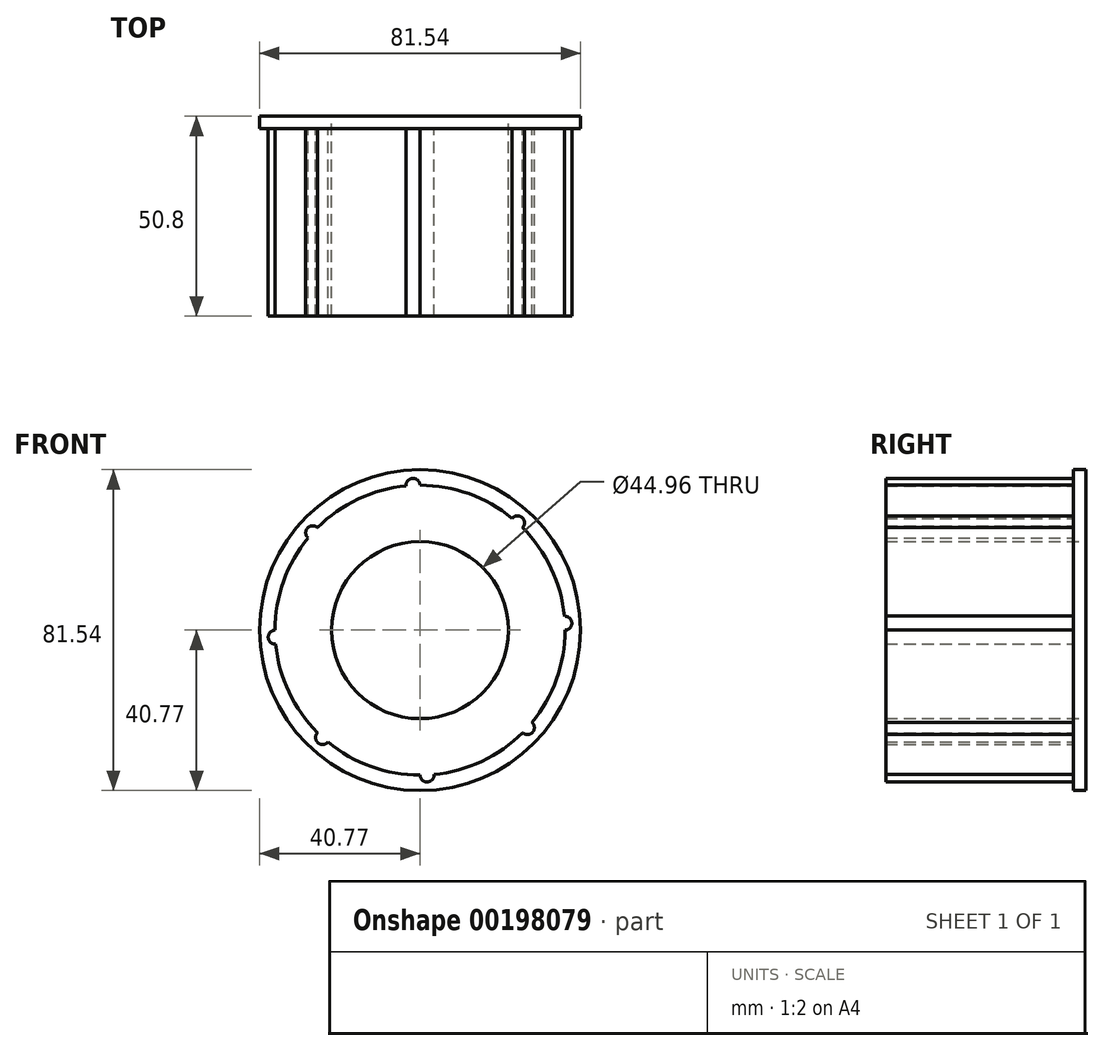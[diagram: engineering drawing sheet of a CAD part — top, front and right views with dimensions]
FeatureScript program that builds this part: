
annotation { "Feature Type Name" : "Feature", "Feature Type Description" : "" }
export const myFeature = defineFeature(function(context is Context, id is Id, definition is map)
    precondition{}
    {
        {
            var Q0;
            Q0=qCreatedBy(makeId("Front.planeOp"),FACE);
            var sketch = newSketch(context, id + "F0", { "sketchPlane" : qUnion([Q0])});
            skCircle(sketch, "E0", {"center": v(0, 0) * mm, "radius": 36.83 * mm});
            skCircle(sketch, "E1", {"center": v(0, 0) * mm, "radius": 22.48 * mm});
            skCircle(sketch, "E2", {"center": v(0, 0) * mm, "radius": 40.77 * mm});
            skArc(sketch, "E3", {"start": v(0, 36.83) * mm, "mid": v(-1.86, 38.56) * mm, "end": v(-3.55, 36.66) * mm});
            skArc(sketch, "E4.1.0", {"start": v(-26.04, 26.04) * mm, "mid": v(-28.59, 25.95) * mm, "end": v(-28.43, 23.41) * mm});
            skArc(sketch, "E4.2.0", {"start": v(-36.83, 0) * mm, "mid": v(-38.56, -1.86) * mm, "end": v(-36.66, -3.55) * mm});
            skArc(sketch, "E4.3.0", {"start": v(-26.04, -26.04) * mm, "mid": v(-25.95, -28.59) * mm, "end": v(-23.41, -28.43) * mm});
            skArc(sketch, "E4.4.0", {"start": v(0, -36.83) * mm, "mid": v(1.86, -38.56) * mm, "end": v(3.55, -36.66) * mm});
            skArc(sketch, "E4.5.0", {"start": v(26.04, -26.04) * mm, "mid": v(28.59, -25.95) * mm, "end": v(28.43, -23.41) * mm});
            skArc(sketch, "E4.6.0", {"start": v(36.83, 0) * mm, "mid": v(38.56, 1.86) * mm, "end": v(36.66, 3.55) * mm});
            skArc(sketch, "E4.7.0", {"start": v(26.04, 26.04) * mm, "mid": v(25.95, 28.59) * mm, "end": v(23.41, 28.43) * mm});
            skSolve(sketch);
        }
        {
            var Q0;
            Q0=makeQuery(id+"F0.imprint","IMPRINT",FACE,{"disambiguationData":[TD([[makeQuery(id+"F0.imprint","IMPRINT",EDGE,{"derivedFrom":sQuery(id+"F0.wireOp",EDGE,"E1")}),-1.0]])]});
            var Q1;
            {var subQ0=sQuery(id+"F0.wireOp",EDGE,"E3");Q1=makeQuery(id+"F0.imprint","IMPRINT",FACE,{"disambiguationData":[TD([[makeQuery(id+"F0.imprint","IMPRINT",EDGE,{"derivedFrom":subQ0}),1.0]])]});}
            var Q2;
            {var subQ0=sQuery(id+"F0.wireOp",EDGE,"E4.1.0");Q2=makeQuery(id+"F0.imprint","IMPRINT",FACE,{"disambiguationData":[TD([[makeQuery(id+"F0.imprint","IMPRINT",EDGE,{"derivedFrom":subQ0}),1.0]])]});}
            var Q3;
            {var subQ0=sQuery(id+"F0.wireOp",EDGE,"E4.2.0");Q3=makeQuery(id+"F0.imprint","IMPRINT",FACE,{"disambiguationData":[TD([[makeQuery(id+"F0.imprint","IMPRINT",EDGE,{"derivedFrom":subQ0}),1.0]])]});}
            var Q4;
            {var subQ0=sQuery(id+"F0.wireOp",EDGE,"E4.6.0");Q4=makeQuery(id+"F0.imprint","IMPRINT",FACE,{"disambiguationData":[TD([[makeQuery(id+"F0.imprint","IMPRINT",EDGE,{"derivedFrom":subQ0}),1.0]])]});}
            var Q5;
            {var subQ0=sQuery(id+"F0.wireOp",EDGE,"E4.7.0");Q5=makeQuery(id+"F0.imprint","IMPRINT",FACE,{"disambiguationData":[TD([[makeQuery(id+"F0.imprint","IMPRINT",EDGE,{"derivedFrom":subQ0}),1.0]])]});}
            var Q6;
            {var subQ0=sQuery(id+"F0.wireOp",EDGE,"E4.5.0");Q6=makeQuery(id+"F0.imprint","IMPRINT",FACE,{"disambiguationData":[TD([[makeQuery(id+"F0.imprint","IMPRINT",EDGE,{"derivedFrom":subQ0}),1.0]])]});}
            var Q7;
            {var subQ0=sQuery(id+"F0.wireOp",EDGE,"E4.4.0");Q7=makeQuery(id+"F0.imprint","IMPRINT",FACE,{"disambiguationData":[TD([[makeQuery(id+"F0.imprint","IMPRINT",EDGE,{"derivedFrom":subQ0}),1.0]])]});}
            var Q8;
            {var subQ0=sQuery(id+"F0.wireOp",EDGE,"E4.3.0");Q8=makeQuery(id+"F0.imprint","IMPRINT",FACE,{"disambiguationData":[TD([[makeQuery(id+"F0.imprint","IMPRINT",EDGE,{"derivedFrom":subQ0}),1.0]])]});}
            extrude(context, id + "F1", {"entities" : qUnion([Q0, Q1, Q2, Q3, Q4, Q5, Q6, Q7, Q8]), "depth" : 50.8 * mm});
        }
        {
            var Q0;
            {var subQ7=sQuery(id+"F0.wireOp",EDGE,"E3");Q0=makeQuery(id+"F0.imprint","IMPRINT",FACE,{"disambiguationData":[TD([[makeQuery(id+"F0.imprint","IMPRINT",EDGE,{"derivedFrom":subQ7}),-1.0]])]});}
            extrude(context, id + "F2", {"entities" : qUnion([Q0]), "operationType" : NewBodyOperationType.ADD, "depth" : 3.17 * mm});
        }
    });
